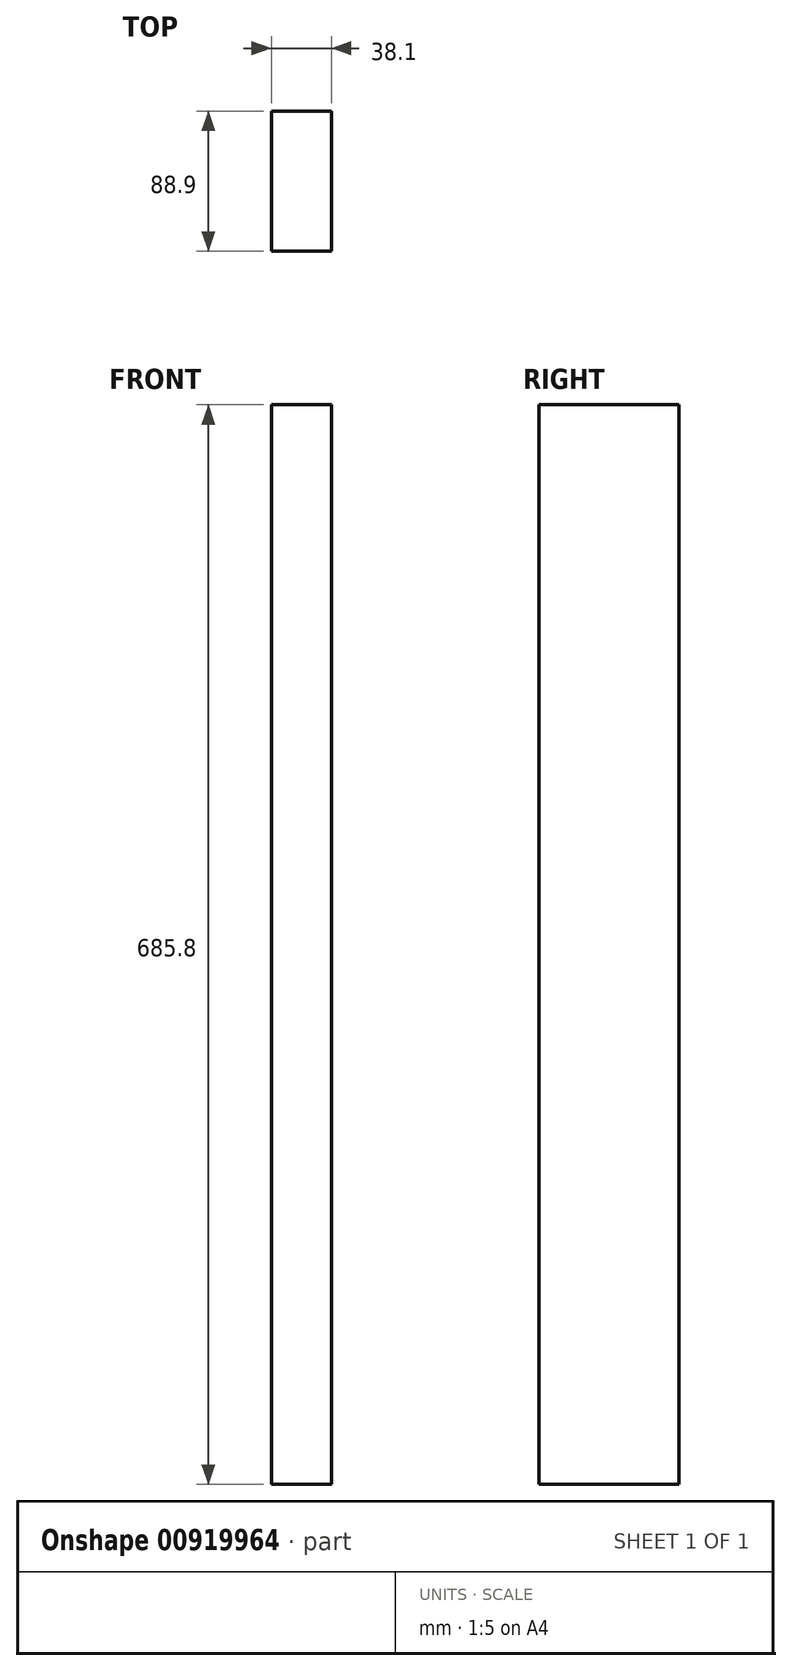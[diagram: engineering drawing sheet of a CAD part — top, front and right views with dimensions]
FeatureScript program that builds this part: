
annotation { "Feature Type Name" : "Feature", "Feature Type Description" : "" }
export const myFeature = defineFeature(function(context is Context, id is Id, definition is map)
    precondition{}
    {
        {
            var Q0;
            Q0=qCreatedBy(makeId("Top.planeOp"),FACE);
            var sketch = newSketch(context, id + "F0", { "sketchPlane" : qUnion([Q0])});
            skLineSegment(sketch, "E0.bottom", {"start": v(-19.05, 44.45) * mm, "end": v(19.05, 44.45) * mm});
            skLineSegment(sketch, "E0.top", {"start": v(-19.05, -44.45) * mm, "end": v(19.05, -44.45) * mm});
            skLineSegment(sketch, "E0.left", {"start": v(-19.05, 44.45) * mm, "end": v(-19.05, -44.45) * mm});
            skLineSegment(sketch, "E0.right", {"start": v(19.05, 44.45) * mm, "end": v(19.05, -44.45) * mm});
            skPoint(sketch, "E1", {"position": v(0, 44.45) * mm});
            skPoint(sketch, "E2", {"position": v(19.05, 0) * mm});
            skSolve(sketch);
        }
        {
            var Q0;
            Q0=qSketchRegion(id+"F0",true);
            extrude(context, id + "F1", {"entities" : qUnion([Q0]), "depth" : 762 * mm - 76.2 * mm, "offsetDistance" : 25 * mm});
        }
    });
